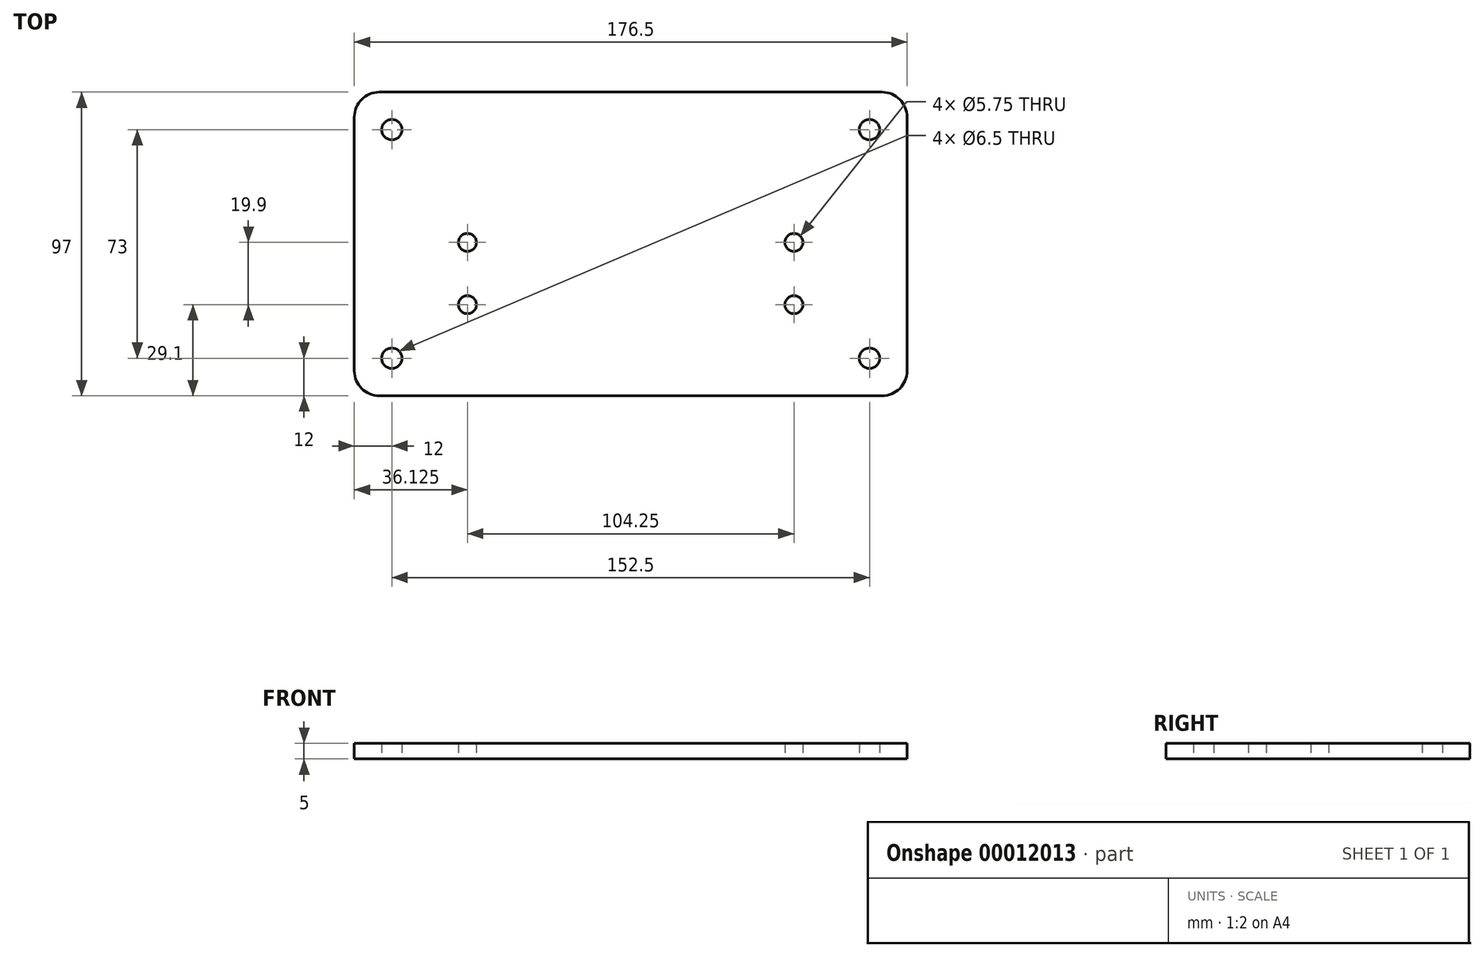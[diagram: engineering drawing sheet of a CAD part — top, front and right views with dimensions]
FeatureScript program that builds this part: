
annotation { "Feature Type Name" : "Feature", "Feature Type Description" : "" }
export const myFeature = defineFeature(function(context is Context, id is Id, definition is map)
    precondition{}
    {
        {
            var Q0;
            Q0=qCreatedBy(makeId("Top.planeOp"),FACE);
            var sketch = newSketch(context, id + "F0", { "sketchPlane" : qUnion([Q0])});
            skCircle(sketch, "E0", {"center": v(-52.12, 9.95) * mm, "radius": 2.88 * mm});
            skCircle(sketch, "E1", {"center": v(-52.12, -9.95) * mm, "radius": 2.88 * mm});
            skCircle(sketch, "E2", {"center": v(-76.25, 45.95) * mm, "radius": 3.25 * mm});
            skCircle(sketch, "E3", {"center": v(-76.25, -27.05) * mm, "radius": 3.25 * mm});
            skCircle(sketch, "E4.0.MirrorC", {"center": v(52.12, 9.95) * mm, "radius": 2.88 * mm});
            skCircle(sketch, "E4.1.MirrorC", {"center": v(76.25, 45.95) * mm, "radius": 3.25 * mm});
            skCircle(sketch, "E4.2.MirrorC", {"center": v(52.12, -9.95) * mm, "radius": 2.88 * mm});
            skCircle(sketch, "E4.3.MirrorC", {"center": v(76.25, -27.05) * mm, "radius": 3.25 * mm});
            skLineSegment(sketch, "E5.rect.bottom", {"start": v(80.25, -39.05) * mm, "end": v(-80.25, -39.05) * mm});
            skLineSegment(sketch, "E5.rect.top", {"start": v(80.25, 57.95) * mm, "end": v(-80.25, 57.95) * mm});
            skLineSegment(sketch, "E5.rect.left", {"start": v(88.25, -31.05) * mm, "end": v(88.25, 49.95) * mm});
            skLineSegment(sketch, "E5.rect.right", {"start": v(-88.25, -31.05) * mm, "end": v(-88.25, 49.95) * mm});
            skPoint(sketch, "E5.rect.middle", {"position": v(0, 9.45) * mm});
            skPoint(sketch, "E6.visualSharp", {"position": v(-88.25, 57.95) * mm});
            skArc(sketch, "E6.filletArc", {"start": v(-80.25, 57.95) * mm, "mid": v(-85.9, 55.6) * mm, "end": v(-88.25, 49.95) * mm});
            skPoint(sketch, "E7.visualSharp", {"position": v(88.25, 57.95) * mm});
            skArc(sketch, "E7.filletArc", {"start": v(88.25, 49.95) * mm, "mid": v(85.9, 55.6) * mm, "end": v(80.25, 57.95) * mm});
            skPoint(sketch, "E8.visualSharp", {"position": v(88.25, -39.05) * mm});
            skArc(sketch, "E8.filletArc", {"start": v(80.25, -39.05) * mm, "mid": v(85.9, -36.7) * mm, "end": v(88.25, -31.05) * mm});
            skPoint(sketch, "E9.visualSharp", {"position": v(-88.25, -39.05) * mm});
            skArc(sketch, "E9.filletArc", {"start": v(-88.25, -31.05) * mm, "mid": v(-85.9, -36.7) * mm, "end": v(-80.25, -39.05) * mm});
            skSolve(sketch);
        }
        {
            var Q0;
            Q0 = qSketchRegion(id + "F0", true);
            extrude(context, id + "F1", {"entities" : qUnion([Q0]), "depth" : 5 * mm});
        }
    });
